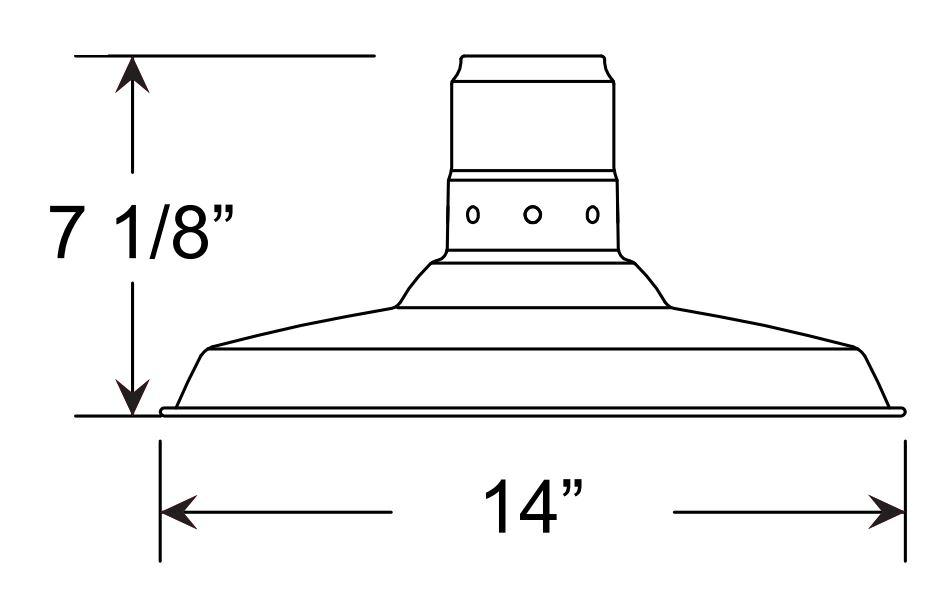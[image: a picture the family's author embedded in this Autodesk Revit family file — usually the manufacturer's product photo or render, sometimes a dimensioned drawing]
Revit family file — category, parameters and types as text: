
# Revit family: OSGGF Metal Fabric LED 24,30,36
name_source: partatom
category: Lighting Fixtures
units: mm (PartAtom-declared; Revit-internal decimal feet)

## family parameters
Always vertical = Yes
Cut with Voids When Loaded = No
Light Source = Yes
OmniClass Number = 23.80.70.00
OmniClass Title = Lighting
Part Type = Normal
Room Calculation Point = No
Round Connector Dimension = Use Diameter
Shared = No
Work Plane-Based = No

## types (3) — shared parameters
Apparent Load = 24 VA
Body Colour = Spun aluminium
Body Material = body
Bulb = Glass
CRI = >90
Canopy Body = GY
Color Filter = 16777215
Construction Material = Heavy Duty spun aluminum.
Default Elevation = 0' - 0"
Description = 120-277 Voltage
Dimming = 1%
Dimming Lamp Color Temperature Shift = <None>
Efficiency = 97-125 lumens per watt
HUB = Black
Lamp = LED
Life = L70 50,000 hours
Load Classification = Lighting
Manufacturer = ANP Lighting
Photometric Web File = generic
Power Factor = 1
Tilt Angle = 90.00°
URL = https://www.anplighting.com
Voltage = 120 V
Warranty = 5 year limited warranty
b = 0' - 3"

## per-type parameters (varying)
| type | Fixture Diameter | Fixture Height | OSGGF24 | OSGGF30 | OSGGF36 | Wattage Comments | Weight | a |
| OSGGF24 | 2' - 0" | 2' - 2 1/2" | Yes | No | No | 24 W | 11.0 lbs | 1' - 10" |
| OSGGF30 | 2' - 6" | 2' - 9" | No | Yes | No | 24W | 16.5 lbs | 2' - 0" |
| OSGGF36 | 3' - 0" | 3' - 3 3/4" | No | No | Yes | 24W | 16.5 lbs | 2' - 4" |

note: column(s) folded — value = type name in every type: Model

## geometry (parser evidence)
native form markers: Sweep x35
no freeform markers — native parametric forms only
